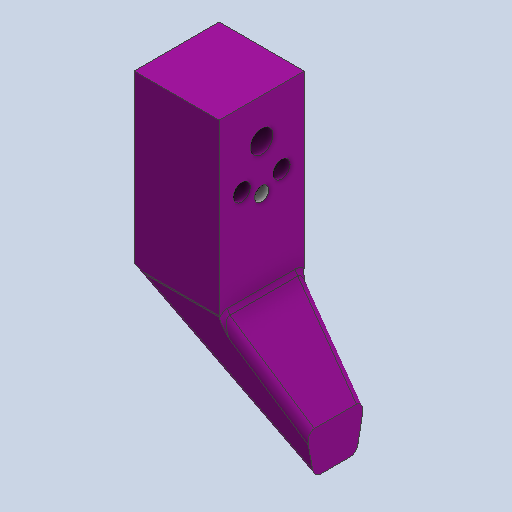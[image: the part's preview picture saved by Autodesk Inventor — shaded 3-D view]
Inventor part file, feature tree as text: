
AUTODESK INVENTOR PART (.ipt)
format: ipt  version: 2025.1 (Build 291241020, 241B)  size: 336,384 bytes
history: native  units: in
note: dims shown in document units (in); Inventor stores cm internally (conversion verified against a paired STEP export)
features: extrude x5, sketch x5, fillet x1
ambient origin geometry x8: Origin, YZ Plane, XZ Plane, XY Plane, X Axis, Y Axis, Z Axis, Center Point
bodies: Solid1 (feature_tree)
feature tree (11):
  extrude  "Extrusion1"  Depth=1.5in
  extrude  "Extrusion2"  Depth=2.0in
  extrude  "Extrusion3"  Depth=1.5in TaperAngle=0.0deg
  fillet  "Fillet1"  Radius=0.375in
  extrude  "Extrusion4"  Depth=1.3in
  extrude  "Extrusion5"  Depth=0.1875in
  sketch  "Sketch1"  dims[d0=3.0in d1=1.5in]
  sketch  "Sketch3"  dims[d3=2.8in d4=2.0in]
  sketch  "Sketch4"  dims[d5=0.75in d6=1.5in d7=0.0in d9=0.375in]
  sketch  "Sketch5"  dims[d10=1.5in d11=0.0in d12=1.3in]
  sketch  "Sketch6"  dims[d13=0.3976in d14=0.7in d15=1.0in d16=0.0in d17=0.125in d18=0.1875in d19=0.1875in d20=0.4in d21=0.4in d22=1.3in d23=1.0in d24=0.0in d25=0.3in d26=0.1875in d27=0.0in d28=0.25in d29=1.5in d30=0.8in d31=0.6in]
